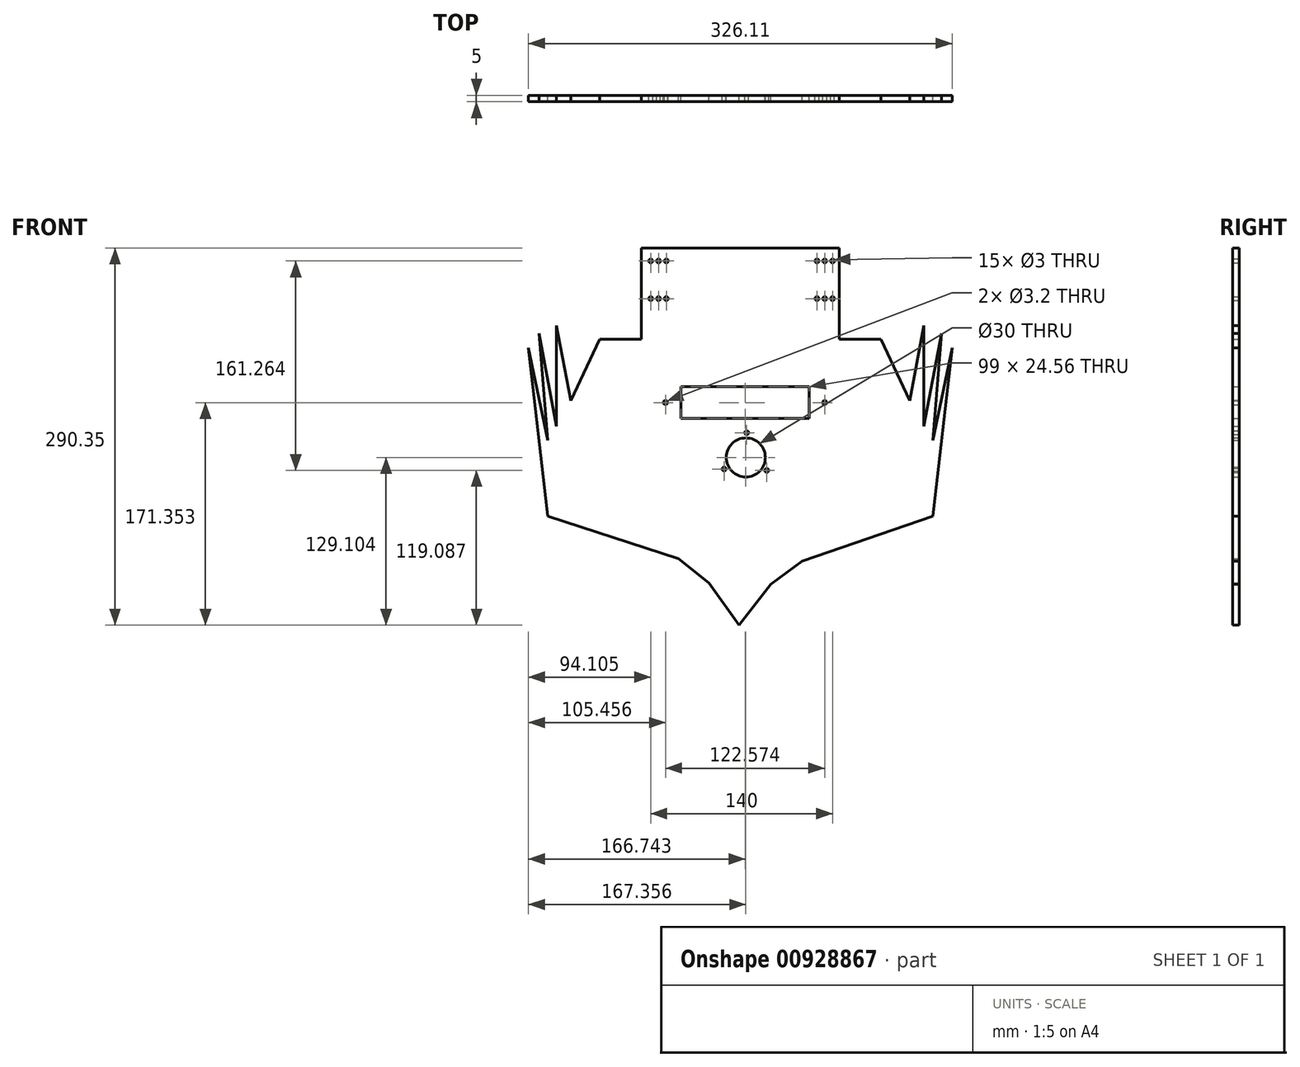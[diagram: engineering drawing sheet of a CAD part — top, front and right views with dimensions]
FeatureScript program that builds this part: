
annotation { "Feature Type Name" : "Feature", "Feature Type Description" : "" }
export const myFeature = defineFeature(function(context is Context, id is Id, definition is map)
    precondition{}
    {
        {
            var Q0;
            Q0=qCreatedBy(makeId("Front.planeOp"),FACE);
            var sketch = newSketch(context, id + "F0", { "sketchPlane" : qUnion([Q0])});
            skCircle(sketch, "E0", {"center": v(-87.86, 37.83) * mm, "radius": 1.5 * mm});
            skCircle(sketch, "E1.0.1.0", {"center": v(-87.86, 66.83) * mm, "radius": 1.5 * mm});
            skCircle(sketch, "E1.1.0.0", {"center": v(-81.86, 37.83) * mm, "radius": 1.5 * mm});
            skCircle(sketch, "E1.1.1.0", {"center": v(-81.86, 66.83) * mm, "radius": 1.5 * mm});
            skCircle(sketch, "E1.2.0.0", {"center": v(-75.86, 37.83) * mm, "radius": 1.5 * mm});
            skCircle(sketch, "E1.2.1.0", {"center": v(-75.86, 66.83) * mm, "radius": 1.5 * mm});
            skLineSegment(sketch, "E1.direction1", {"start": v(-87.86, 37.83) * mm, "end": v(-81.86, 37.83) * mm, "construction": true});
            skLineSegment(sketch, "E1.direction2", {"start": v(-87.86, 37.83) * mm, "end": v(-87.86, 66.83) * mm, "construction": true});
            skLineSegment(sketch, "E2", {"start": v(-17.86, 40.84) * mm, "end": v(-17.86, 68.64) * mm});
            skCircle(sketch, "E3.MirrorC", {"center": v(52.14, 66.83) * mm, "radius": 1.5 * mm});
            skLineSegment(sketch, "E4.MirrorCS", {"start": v(52.14, 37.83) * mm, "end": v(46.14, 37.83) * mm, "construction": true});
            skCircle(sketch, "E5.MirrorC", {"center": v(40.14, 37.83) * mm, "radius": 1.5 * mm});
            skCircle(sketch, "E6.MirrorC", {"center": v(52.14, 37.83) * mm, "radius": 1.5 * mm});
            skCircle(sketch, "E7.MirrorC", {"center": v(46.14, 37.83) * mm, "radius": 1.5 * mm});
            skCircle(sketch, "E8.MirrorC", {"center": v(46.14, 66.83) * mm, "radius": 1.5 * mm});
            skCircle(sketch, "E9.MirrorC", {"center": v(40.14, 66.83) * mm, "radius": 1.5 * mm});
            skLineSegment(sketch, "E10.MirrorCS", {"start": v(52.14, 37.83) * mm, "end": v(52.14, 66.83) * mm, "construction": true});
            skLineSegment(sketch, "E11.bottom", {"start": v(-95.22, 76.83) * mm, "end": v(57.38, 76.83) * mm});
            skLineSegment(sketch, "E11.left", {"start": v(-95.22, 76.83) * mm, "end": v(-95.22, -129.75) * mm});
            skLineSegment(sketch, "E11.right", {"start": v(57.38, 76.83) * mm, "end": v(57.38, -129.75) * mm});
            skPoint(sketch, "E12", {"position": v(-87.32, 76.83) * mm});
            skCircle(sketch, "E13", {"center": v(-14.61, -84.42) * mm, "radius": 15 * mm});
            skLineSegment(sketch, "E14", {"start": v(-80.51, -42.17) * mm, "end": v(-64.73, -29.89) * mm});
            skLineSegment(sketch, "E15", {"start": v(-64.73, -29.89) * mm, "end": v(34.27, -29.89) * mm});
            skLineSegment(sketch, "E16", {"start": v(34.27, -29.89) * mm, "end": v(50.06, -42.17) * mm});
            skLineSegment(sketch, "E17", {"start": v(50.06, -42.17) * mm, "end": v(34.27, -54.45) * mm});
            skLineSegment(sketch, "E18", {"start": v(34.27, -54.45) * mm, "end": v(-64.73, -54.45) * mm});
            skLineSegment(sketch, "E19", {"start": v(-64.73, -54.45) * mm, "end": v(-80.51, -42.17) * mm});
            skLineSegment(sketch, "E20", {"start": v(-64.73, -29.89) * mm, "end": v(-64.73, -54.45) * mm});
            skLineSegment(sketch, "E21", {"start": v(34.27, -29.89) * mm, "end": v(34.27, -54.45) * mm});
            skCircle(sketch, "E22", {"center": v(-76.51, -42.17) * mm, "radius": 1.6 * mm});
            skCircle(sketch, "E23", {"center": v(46.06, -42.17) * mm, "radius": 1.6 * mm});
            skLineSegment(sketch, "E24", {"start": v(-14.61, -84.42) * mm, "end": v(32.92, -84.42) * mm});
            skPoint(sketch, "E25.start.orphan", {"position": v(-95.22, 6.5) * mm});
            skPoint(sketch, "E26.start.orphan", {"position": v(57.38, 6.5) * mm});
            skLineSegment(sketch, "E27", {"start": v(-95.22, 6.5) * mm, "end": v(-127.22, 6.5) * mm});
            skLineSegment(sketch, "E28", {"start": v(-127.22, 6.5) * mm, "end": v(-167.2, -129.75) * mm});
            skLineSegment(sketch, "E29", {"start": v(-167.2, -129.75) * mm, "end": v(-66.61, -162.28) * mm});
            skLineSegment(sketch, "E30", {"start": v(28.8, -164.18) * mm, "end": v(129.38, -129.75) * mm});
            skLineSegment(sketch, "E31", {"start": v(129.38, -129.75) * mm, "end": v(89.38, 6.5) * mm});
            skLineSegment(sketch, "E32", {"start": v(89.38, 6.5) * mm, "end": v(57.38, 6.5) * mm});
            skLineSegment(sketch, "E33", {"start": v(-95.22, -129.75) * mm, "end": v(-66.61, -162.28) * mm});
            skLineSegment(sketch, "E34", {"start": v(28.8, -164.18) * mm, "end": v(57.38, -129.75) * mm});
            skLineSegment(sketch, "E35", {"start": v(28.8, -164.18) * mm, "end": v(-19.2, -178.18) * mm});
            skLineSegment(sketch, "E36", {"start": v(-19.2, -178.18) * mm, "end": v(-66.61, -162.28) * mm});
            skLineSegment(sketch, "E37", {"start": v(129.38, -129.75) * mm, "end": v(144.14, 0) * mm});
            skLineSegment(sketch, "E38", {"start": v(144.14, 0) * mm, "end": v(129.38, -71.12) * mm});
            skLineSegment(sketch, "E39", {"start": v(129.38, -71.12) * mm, "end": v(136.02, 10.98) * mm});
            skLineSegment(sketch, "E40", {"start": v(136.02, 10.98) * mm, "end": v(122.53, -60.3) * mm});
            skLineSegment(sketch, "E41", {"start": v(122.53, -60.3) * mm, "end": v(122.53, 17.08) * mm});
            skLineSegment(sketch, "E42", {"start": v(122.53, 17.08) * mm, "end": v(111.5, -40.77) * mm});
            skLineSegment(sketch, "E43", {"start": v(111.5, -40.77) * mm, "end": v(89.38, 6.5) * mm});
            skLineSegment(sketch, "E44", {"start": v(-18.92, -262.46) * mm, "end": v(-18.92, -262.34) * mm});
            skLineSegment(sketch, "E45.MirrorCS", {"start": v(-127.22, 6.5) * mm, "end": v(-95.22, 6.5) * mm});
            skLineSegment(sketch, "E46.MirrorCS", {"start": v(-149.33, -40.77) * mm, "end": v(-127.22, 6.5) * mm});
            skLineSegment(sketch, "E47.MirrorCS", {"start": v(-167.2, -129.75) * mm, "end": v(-181.97, 0) * mm});
            skLineSegment(sketch, "E48.MirrorCS", {"start": v(-160.36, 17.08) * mm, "end": v(-149.33, -40.77) * mm});
            skLineSegment(sketch, "E49.MirrorCS", {"start": v(-160.36, -60.3) * mm, "end": v(-160.36, 17.08) * mm});
            skLineSegment(sketch, "E50.MirrorCS", {"start": v(-167.2, -129.75) * mm, "end": v(-127.22, 6.5) * mm});
            skLineSegment(sketch, "E51.MirrorCS", {"start": v(-167.2, -71.12) * mm, "end": v(-173.85, 10.98) * mm});
            skLineSegment(sketch, "E52.MirrorCS", {"start": v(-181.97, 0) * mm, "end": v(-167.2, -71.12) * mm});
            skLineSegment(sketch, "E53.MirrorCS", {"start": v(-95.22, 76.83) * mm, "end": v(-95.22, -67.65) * mm});
            skLineSegment(sketch, "E54.MirrorCS", {"start": v(-173.85, 10.98) * mm, "end": v(-160.36, -60.3) * mm});
            skPoint(sketch, "E55.trimOffspring.end.orphan", {"position": v(-17.86, 87.1) * mm});
            skLineSegment(sketch, "E56", {"start": v(-95.22, -129.75) * mm, "end": v(57.38, -129.75) * mm});
            skLineSegment(sketch, "E57", {"start": v(89.38, 6.5) * mm, "end": v(57.38, -129.75) * mm});
            skLineSegment(sketch, "E58", {"start": v(-127.22, 6.5) * mm, "end": v(-95.22, -129.75) * mm});
            skPoint(sketch, "E59.end.orphan", {"position": v(20.33, -174.37) * mm});
            skPoint(sketch, "E60.start.orphan", {"position": v(-16.73, -233.03) * mm});
            skPoint(sketch, "E61.orphan", {"position": v(-16.73, -219) * mm});
            skLineSegment(sketch, "E62", {"start": v(-66.61, -162.28) * mm, "end": v(-19.63, -199.6) * mm});
            skLineSegment(sketch, "E63", {"start": v(-19.63, -199.6) * mm, "end": v(28.8, -164.18) * mm});
            skLineSegment(sketch, "E64", {"start": v(-43.12, -180.94) * mm, "end": v(-19.9, -213.52) * mm});
            skLineSegment(sketch, "E65", {"start": v(-19.9, -213.52) * mm, "end": v(4.58, -181.89) * mm});
            skCircle(sketch, "E66", {"center": v(-14.01, -65.43) * mm, "radius": 1.5 * mm});
            skCircle(sketch, "E67.1.0", {"center": v(-31.36, -93.39) * mm, "radius": 1.5 * mm});
            skCircle(sketch, "E67.2.0", {"center": v(1.53, -94.43) * mm, "radius": 1.5 * mm});
            skSolve(sketch);
        }
        {
            var Q0;
            Q0=makeQuery(id+"F0.imprint","IMPRINT",FACE,{"disambiguationData":[TD([[makeQuery(id+"F0.imprint","IMPRINT",EDGE,{"derivedFrom":sQuery(id+"F0.wireOp",EDGE,"E29")}),1.0]])]});
            var Q1;
            Q1=makeQuery(id+"F0.imprint","IMPRINT",FACE,{"disambiguationData":[TD([[makeQuery(id+"F0.imprint","IMPRINT",EDGE,{"derivedFrom":sQuery(id+"F0.wireOp",EDGE,"E46.MirrorCS")}),-1.0]])]});
            var Q2;
            {var subQ0=sQuery(id+"F0.wireOp",EDGE,"E11.left");Q2=makeQuery(id+"F0.imprint","IMPRINT",FACE,{"disambiguationData":[TD([[makeQuery(id+"F0.imprint","IMPRINT",EDGE,{"derivedFrom":subQ0}),-1.0]])]});}
            var Q3;
            Q3=makeQuery(id+"F0.imprint","IMPRINT",FACE,{"disambiguationData":[TD([[makeQuery(id+"F0.imprint","IMPRINT",EDGE,{"derivedFrom":sQuery(id+"F0.wireOp",EDGE,"E0")}),-1.0]])]});
            var Q4;
            {var subQ5=sQuery(id+"F0.wireOp",EDGE,"E35");Q4=makeQuery(id+"F0.imprint","IMPRINT",FACE,{"disambiguationData":[TD([[makeQuery(id+"F0.imprint","IMPRINT",EDGE,{"derivedFrom":subQ5}),1.0]])]});}
            var Q5;
            Q5=makeQuery(id+"F0.imprint","IMPRINT",FACE,{"disambiguationData":[TD([[makeQuery(id+"F0.imprint","IMPRINT",EDGE,{"derivedFrom":sQuery(id+"F0.wireOp",EDGE,"E33")}),1.0]])]});
            var Q6;
            {var subQ3=sQuery(id+"F0.wireOp",EDGE,"E64");Q6=makeQuery(id+"F0.imprint","IMPRINT",FACE,{"disambiguationData":[TD([[makeQuery(id+"F0.imprint","IMPRINT",EDGE,{"derivedFrom":subQ3}),1.0]])]});}
            var Q7;
            Q7=makeQuery(id+"F0.imprint","IMPRINT",FACE,{"disambiguationData":[TD([[makeQuery(id+"F0.imprint","IMPRINT",EDGE,{"derivedFrom":sQuery(id+"F0.wireOp",EDGE,"E30")}),1.0]])]});
            var Q8;
            {var subQ2=sQuery(id+"F0.wireOp",EDGE,"E32");Q8=makeQuery(id+"F0.imprint","IMPRINT",FACE,{"disambiguationData":[TD([[makeQuery(id+"F0.imprint","IMPRINT",EDGE,{"derivedFrom":subQ2}),1.0]])]});}
            var Q9;
            Q9=makeQuery(id+"F0.imprint","IMPRINT",FACE,{"disambiguationData":[TD([[makeQuery(id+"F0.imprint","IMPRINT",EDGE,{"derivedFrom":sQuery(id+"F0.wireOp",EDGE,"E31")}),-1.0]])]});
            var Q10;
            Q10=makeQuery(id+"F0.imprint","IMPRINT",FACE,{"disambiguationData":[TD([[makeQuery(id+"F0.imprint","IMPRINT",EDGE,{"derivedFrom":sQuery(id+"F0.wireOp",EDGE,"E14")}),-1.0]])]});
            var Q11;
            Q11=makeQuery(id+"F0.imprint","IMPRINT",FACE,{"disambiguationData":[TD([[makeQuery(id+"F0.imprint","IMPRINT",EDGE,{"derivedFrom":sQuery(id+"F0.wireOp",EDGE,"E16")}),-1.0]])]});
            extrude(context, id + "F1", {"entities" : qUnion([Q0, Q1, Q2, Q3, Q4, Q5, Q6, Q7, Q8, Q9, Q10, Q11]), "depth" : 5 * mm, "offsetDistance" : 25 * mm});
        }
    });
